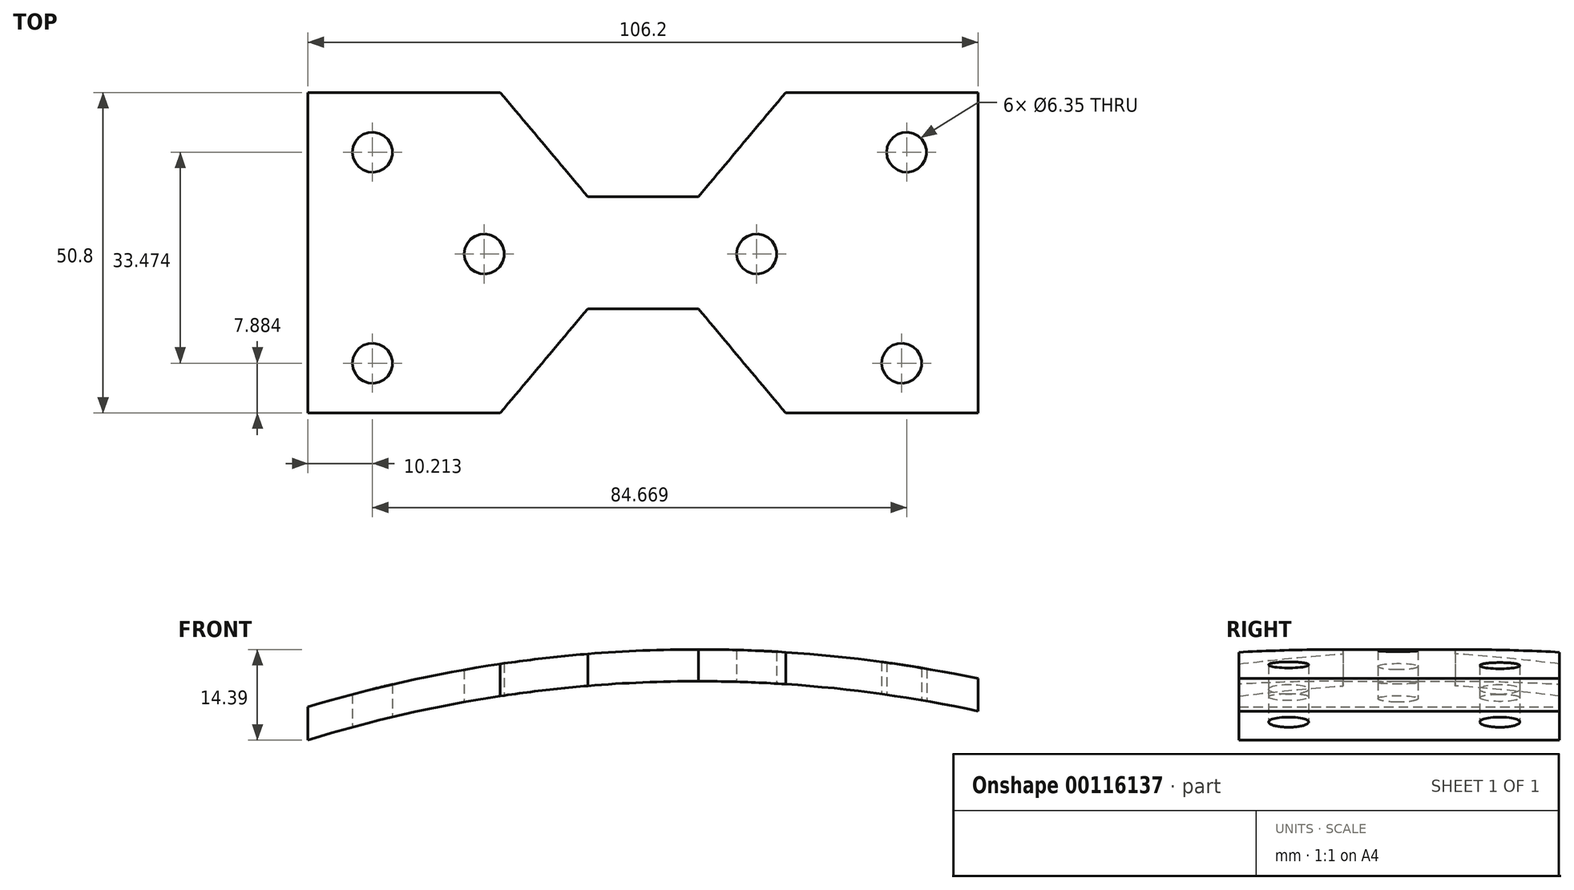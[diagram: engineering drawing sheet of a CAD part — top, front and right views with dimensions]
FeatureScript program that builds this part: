
annotation { "Feature Type Name" : "Feature", "Feature Type Description" : "" }
export const myFeature = defineFeature(function(context is Context, id is Id, definition is map)
    precondition{}
    {
        {
            var Q0;
            Q0=qCreatedBy(makeId("Front.planeOp"),FACE);
            var sketch = newSketch(context, id + "F0", { "sketchPlane" : qUnion([Q0])});
            skArc(sketch, "E0", {"start": v(209.55, 0) * mm, "mid": v(0, 209.55) * mm, "end": v(-209.55, 0) * mm});
            skArc(sketch, "E1", {"start": v(214.6, 0) * mm, "mid": v(0, 214.6) * mm, "end": v(-214.6, 0) * mm});
            skLineSegment(sketch, "E2", {"start": v(-209.55, 0) * mm, "end": v(-214.6, 0) * mm});
            skLineSegment(sketch, "E3", {"start": v(209.55, 0) * mm, "end": v(214.6, 0) * mm});
            skSolve(sketch);
        }
        {
            var Q0;
            Q0 = qSketchRegion(id + "F0", true);
            extrude(context, id + "F1", {"entities" : qUnion([Q0]), "depth" : 85.58 * mm});
        }
        {
            var Q0;
            Q0=qCreatedBy(makeId("Top.planeOp"),FACE);
            var sketch = newSketch(context, id + "F2", { "sketchPlane" : qUnion([Q0])});
            skLineSegment(sketch, "E4", {"start": v(-61.86, -21.53) * mm, "end": v(-61.86, -72.33) * mm});
            skLineSegment(sketch, "E5", {"start": v(-61.86, -72.33) * mm, "end": v(-31.38, -72.33) * mm});
            skLineSegment(sketch, "E6", {"start": v(-31.38, -72.33) * mm, "end": v(-17.52, -55.8) * mm});
            skLineSegment(sketch, "E7", {"start": v(-17.52, -55.8) * mm, "end": v(0, -55.8) * mm});
            skLineSegment(sketch, "E8", {"start": v(0, -55.8) * mm, "end": v(13.86, -72.33) * mm});
            skLineSegment(sketch, "E9", {"start": v(13.86, -72.33) * mm, "end": v(44.34, -72.33) * mm});
            skLineSegment(sketch, "E10", {"start": v(44.34, -72.33) * mm, "end": v(44.34, -21.53) * mm});
            skLineSegment(sketch, "E11", {"start": v(-61.86, -21.53) * mm, "end": v(-31.38, -21.53) * mm});
            skLineSegment(sketch, "E12", {"start": v(-31.38, -21.53) * mm, "end": v(-17.52, -38.05) * mm});
            skLineSegment(sketch, "E13", {"start": v(-17.52, -38.05) * mm, "end": v(0, -38.05) * mm});
            skLineSegment(sketch, "E14", {"start": v(0, -38.05) * mm, "end": v(13.86, -21.53) * mm});
            skLineSegment(sketch, "E15", {"start": v(13.86, -21.53) * mm, "end": v(44.34, -21.53) * mm});
            skLineSegment(sketch, "E16.bottom", {"start": v(-229.97, 28.3) * mm, "end": v(240.69, 28.3) * mm});
            skLineSegment(sketch, "E16.top", {"start": v(-229.97, -103.71) * mm, "end": v(240.69, -103.71) * mm});
            skLineSegment(sketch, "E16.left", {"start": v(-229.97, 28.3) * mm, "end": v(-229.97, -103.71) * mm});
            skLineSegment(sketch, "E16.right", {"start": v(240.69, 28.3) * mm, "end": v(240.69, -103.71) * mm});
            skCircle(sketch, "E17", {"center": v(-56.07, -29.78) * mm, "radius": 3.18 * mm});
            skCircle(sketch, "E18", {"center": v(-56.07, -64.07) * mm, "radius": 3.18 * mm});
            skCircle(sketch, "E19", {"center": v(-35.76, -46.75) * mm, "radius": 3.18 * mm});
            skCircle(sketch, "E20", {"center": v(38.25, -29.78) * mm, "radius": 3.18 * mm});
            skCircle(sketch, "E21", {"center": v(38.01, -64.07) * mm, "radius": 3.18 * mm});
            skCircle(sketch, "E22", {"center": v(13.27, -46.75) * mm, "radius": 3.18 * mm});
            skSolve(sketch);
        }
        {
            var Q0;
            Q0 = qSketchRegion(id + "F2", true);
            extrude(context, id + "F3", {"entities" : qUnion([Q0]), "operationType" : NewBodyOperationType.REMOVE, "depth" : 332.33 * mm});
        }
        {
            var Q0;
            Q0=qCreatedBy(makeId("Top.planeOp"),FACE);
            var sketch = newSketch(context, id + "F4", { "sketchPlane" : qUnion([Q0])});
            skCircle(sketch, "E23", {"center": v(-51.65, -30.97) * mm, "radius": 3.17 * mm});
            skCircle(sketch, "E24", {"center": v(-51.65, -64.45) * mm, "radius": 3.18 * mm});
            skCircle(sketch, "E25", {"center": v(-33.93, -47.12) * mm, "radius": 3.18 * mm});
            skCircle(sketch, "E26", {"center": v(9.26, -47.12) * mm, "radius": 3.18 * mm});
            skCircle(sketch, "E27", {"center": v(33.02, -30.97) * mm, "radius": 3.18 * mm});
            skCircle(sketch, "E28", {"center": v(32.23, -64.45) * mm, "radius": 3.18 * mm});
            skSolve(sketch);
        }
        {
            var Q0;
            Q0 = qSketchRegion(id + "F4", true);
            extrude(context, id + "F5", {"entities" : qUnion([Q0]), "operationType" : NewBodyOperationType.REMOVE, "depth" : 369.06 * mm});
        }
    });
